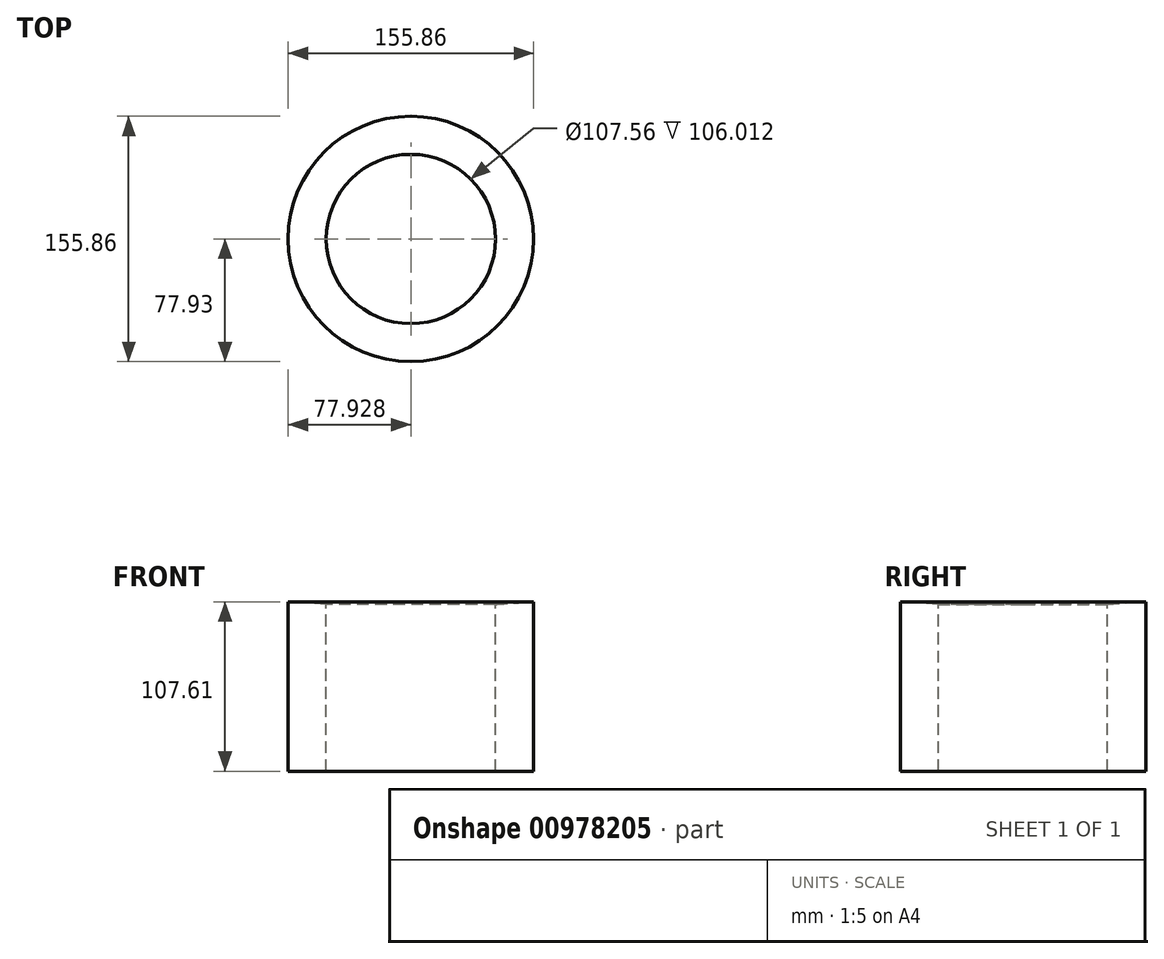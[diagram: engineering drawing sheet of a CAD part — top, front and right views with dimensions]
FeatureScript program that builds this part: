
annotation { "Feature Type Name" : "Feature", "Feature Type Description" : "" }
export const myFeature = defineFeature(function(context is Context, id is Id, definition is map)
    precondition{}
    {
        {
            var Q0;
            Q0=qCreatedBy(makeId("Front.planeOp"),FACE);
            var sketch = newSketch(context, id + "F0", { "sketchPlane" : qUnion([Q0])});
            skLineSegment(sketch, "E0", {"start": v(-52.4, 50.28) * mm, "end": v(-52.4, -57.33) * mm});
            skLineSegment(sketch, "E1", {"start": v(-52.4, -57.33) * mm, "end": v(-52.4, -57.33) * mm});
            skLineSegment(sketch, "E2", {"start": v(-52.4, -57.33) * mm, "end": v(-28.26, -57.33) * mm});
            skLineSegment(sketch, "E3", {"start": v(-28.26, -57.33) * mm, "end": v(-28.26, 48.68) * mm});
            skLineSegment(sketch, "E4", {"start": v(-28.26, 48.68) * mm, "end": v(-52.4, 50.28) * mm});
            skSolve(sketch);
        }
        {
            var Q0;
            Q0=qCreatedBy(makeId("Front.planeOp"),FACE);
            var sketch = newSketch(context, id + "F1", { "sketchPlane" : qUnion([Q0])});
            skLineSegment(sketch, "E5", {"start": v(25.52, 45.34) * mm, "end": v(25.52, -53.49) * mm});
            skSolve(sketch);
        }
        {
            var Q0;
            Q0=makeQuery(id+"F0.imprint","IMPRINT",FACE,{"disambiguationData":[TD([[makeQuery(id+"F0.imprint","IMPRINT",EDGE,{"derivedFrom":sQuery(id+"F0.wireOp",EDGE,"E0")}),1.0]])]});
            var Q1;
            Q1=sQuery(id+"F1.wireOp",EDGE,"E5");
            revolve(context, id + "F2", {"surfaceOperationType" : NewSurfaceOperationType.NEW, "entities" : qUnion([Q0]), "axis" : qUnion([Q1]), "revolveType" : RevolveType.FULL});
        }
    });
